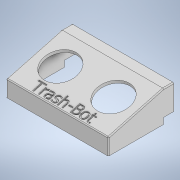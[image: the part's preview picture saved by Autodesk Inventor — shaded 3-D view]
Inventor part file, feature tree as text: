
AUTODESK INVENTOR PART (.ipt)
format: ipt  version: 2020 (Build 240168000, 168)  size: 448,000 bytes
history: native  units: mm
features: sketch x4, extrude x2, shell x1, hole x1, emboss x1, fillet x1
ambient origin geometry x8: Origin, YZ Plane, XZ Plane, XY Plane, X Axis, Y Axis, Z Axis, Center Point
bodies: Solid1 (feature_tree)
feature tree (10):
  extrude  "Extrusion1"  Depth=50.0mm TaperAngle=0.0deg
  shell  "Shell2"  Thickness=5.0mm
  hole  "Hole2"  [1 undecoded]
  emboss  "Emboss1"
  fillet  "Fillet1"  [1 undecoded]
  extrude  "Extrusion3"  Depth=1.5mm
  sketch  "Sketch1"  dims[d8=8.0mm d12=50.0mm d13=0.0mm d26=5.0mm]
  sketch  "Sketch6"  dims[d27=32.0mm d28=15.234628mm d29=75.0deg]
  sketch  "Sketch7"  dims[d30=1.5mm d31=25.999941mm]
  sketch  "Sketch8"  dims[d33=16.0mm d34=6.0mm d35=4.0mm d36=2.0mm d37=90.0deg d38=8.0mm d39=20.594885mm d40=0.5mm d41=0.0mm d42=0.5mm d43=5.0mm d44=3.0mm d45=50.0mm d46=0.0mm d2=0.5mm d3=0.872665mm d4=0.5mm d5=0.872665mm d17=1.0mm d18=1.0mm d19=1.0mm d20=0.15mm d21=0.25mm d22=0.375mm d23=14.3117mm d24=0.75mm d25=20.594885mm]
note: 2 required parameter values undecoded (feature->parameter linkage not recoverable at this tier; creation-order binding heuristic only, values carry confidence <= 0.55)
